# Revit family: vanity unit with 2 drawers for consoles with countertop basin ground
name_source: partatom
category: Furniture
units: mm (PartAtom-declared; Revit-internal decimal feet)

## family parameters
Always vertical = Yes
Cut with Voids When Loaded = No
OmniClass Number = 23.21.19.15.33.13
Room Calculation Point = No
Shared = Yes
Work Plane-Based = No

## types (48) — shared parameters
BIMOBJECT = Sanitary: Compound units
CATALOG = Hansgrohe
DESIGN = Germany
ETIM = EC011381 | Bathroom furniture set
IFC = Furnishing element
MASTERFORMAT = 12 35 30.23 | Bathroom Casework
Manufacturer = Hansgrohe
NBSYN = $BASENUMBER.-$ARTNR.-$OBERFLAECHE.-$SURFACE.-$LODLEVEL.
NN = Vanity Unit with 2 Drawers for consoles with countertop basin ground
OBJECTTYPE = Object (single object)
OMNICLASS = 23-21 19 15 33 13 | Residential Bathroom Specialty Casework
PRODUCTFAMILY = Xelu Q
PRODUCTGROUP = vanity unit
PRODUCTURL = https://pro.hansgrohe.com
REGIONSET = Worldwide
UNICLASS2015 = Pr_40_30_78_05 | Bathroom furniture
UNICLASS_2015_CODE = 40_30_78_05
UNIFORMATII = E2010 | Fixed Furnishings
UNSPSC = 56 | Furniture and Furnishings
etim7_EC011381 = EC011381

## per-type parameters (varying)
| type | ARTNR | BASENUMBER | GTINCODE | L | LINA | LODLEVEL | Model | NAME | NB | OBERFLAECHE | PERMALINK | SURFACE | WEIGHT |
| Vanity unit 1360_550 with 2 drawers for consoles with countertop basin ground-54066000-High Gloss White-CHROME-200 | 54066000 | Vanity unit 1360/550 with 2 drawers for consoles with countertop basin ground | 4059625456378 | 1360 | Vanity unit 1360/550 with 2 drawers for consoles with countertop basin ground-54066000-High Gloss White-CHROME-200 | 200 | Vanity unit 1360/550 with 2 drawers for consoles with countertop basin ground-54066000-High Gloss White-CHROME-200 | Xelu Q Vanity unit High Gloss White 1360/550 with 2 drawers for consoles with countertop basin ground | Vanity unit 1360/550 with 2 drawers for consoles with countertop basin ground-54066000-High Gloss White-CHROME-200 | High Gloss White | 54066XXX | CHROME | 45.1 |
| Vanity unit 1360_550 with 2 drawers for consoles with countertop basin ground-54066000-High Gloss White-CHROME-400 | 54066000 | Vanity unit 1360/550 with 2 drawers for consoles with countertop basin ground | 4059625456378 | 1360 | Vanity unit 1360/550 with 2 drawers for consoles with countertop basin ground-54066000-High Gloss White-CHROME-400 | 400 | Vanity unit 1360/550 with 2 drawers for consoles with countertop basin ground-54066000-High Gloss White-CHROME-400 | Xelu Q Vanity unit High Gloss White 1360/550 with 2 drawers for consoles with countertop basin ground | Vanity unit 1360/550 with 2 drawers for consoles with countertop basin ground-54066000-High Gloss White-CHROME-400 | High Gloss White | 54066XXX | CHROME | 45.1 |
| Vanity unit 1360_550 with 2 drawers for consoles with countertop basin ground-54066670-High Gloss White-MATT_BLACK-200 | 54066670 | Vanity unit 1360/550 with 2 drawers for consoles with countertop basin ground | 4059625456378 | 1360 | Vanity unit 1360/550 with 2 drawers for consoles with countertop basin ground-54066670-High Gloss White-MATT_BLACK-200 | 200 | Vanity unit 1360/550 with 2 drawers for consoles with countertop basin ground-54066670-High Gloss White-MATT_BLACK-200 | Xelu Q Vanity unit High Gloss White 1360/550 with 2 drawers for consoles with countertop basin ground | Vanity unit 1360/550 with 2 drawers for consoles with countertop basin ground-54066670-High Gloss White-MATT_BLACK-200 | High Gloss White | 54066XXX | MATT_BLACK | 45.1 |
| Vanity unit 1360_550 with 2 drawers for consoles with countertop basin ground-54066670-High Gloss White-MATT_BLACK-400 | 54066670 | Vanity unit 1360/550 with 2 drawers for consoles with countertop basin ground | 4059625456378 | 1360 | Vanity unit 1360/550 with 2 drawers for consoles with countertop basin ground-54066670-High Gloss White-MATT_BLACK-400 | 400 | Vanity unit 1360/550 with 2 drawers for consoles with countertop basin ground-54066670-High Gloss White-MATT_BLACK-400 | Xelu Q Vanity unit High Gloss White 1360/550 with 2 drawers for consoles with countertop basin ground | Vanity unit 1360/550 with 2 drawers for consoles with countertop basin ground-54066670-High Gloss White-MATT_BLACK-400 | High Gloss White | 54066XXX | MATT_BLACK | 45.1 |
| Vanity unit 1360_550 with 2 drawers for consoles with countertop basin ground-54066700-High Gloss White-MATT_WHITE-200 | 54066700 | Vanity unit 1360/550 with 2 drawers for consoles with countertop basin ground | 4059625456378 | 1360 | Vanity unit 1360/550 with 2 drawers for consoles with countertop basin ground-54066700-High Gloss White-MATT_WHITE-200 | 200 | Vanity unit 1360/550 with 2 drawers for consoles with countertop basin ground-54066700-High Gloss White-MATT_WHITE-200 | Xelu Q Vanity unit High Gloss White 1360/550 with 2 drawers for consoles with countertop basin ground | Vanity unit 1360/550 with 2 drawers for consoles with countertop basin ground-54066700-High Gloss White-MATT_WHITE-200 | High Gloss White | 54066XXX | MATT_WHITE | 45.1 |
| Vanity unit 1360_550 with 2 drawers for consoles with countertop basin ground-54066700-High Gloss White-MATT_WHITE-400 | 54066700 | Vanity unit 1360/550 with 2 drawers for consoles with countertop basin ground | 4059625456378 | 1360 | Vanity unit 1360/550 with 2 drawers for consoles with countertop basin ground-54066700-High Gloss White-MATT_WHITE-400 | 400 | Vanity unit 1360/550 with 2 drawers for consoles with countertop basin ground-54066700-High Gloss White-MATT_WHITE-400 | Xelu Q Vanity unit High Gloss White 1360/550 with 2 drawers for consoles with countertop basin ground | Vanity unit 1360/550 with 2 drawers for consoles with countertop basin ground-54066700-High Gloss White-MATT_WHITE-400 | High Gloss White | 54066XXX | MATT_WHITE | 45.1 |
| Vanity unit 1360_550 with 2 drawers for consoles with countertop basin ground-54067000-Diamond Matt Grey-CHROME-200 | 54067000 | Vanity unit 1360/550 with 2 drawers for consoles with countertop basin ground | 4059625456347 | 1360 | Vanity unit 1360/550 with 2 drawers for consoles with countertop basin ground-54067000-Diamond Matt Grey-CHROME-200 | 200 | Vanity unit 1360/550 with 2 drawers for consoles with countertop basin ground-54067000-Diamond Matt Grey-CHROME-200 | Xelu Q Vanity unit Diamond Matt Grey 1360/550 with 2 drawers for consoles with countertop basin ground | Vanity unit 1360/550 with 2 drawers for consoles with countertop basin ground-54067000-Diamond Matt Grey-CHROME-200 | Diamond Matt Grey | 54067XXX | CHROME | 45.1 |
| Vanity unit 1360_550 with 2 drawers for consoles with countertop basin ground-54067000-Diamond Matt Grey-CHROME-400 | 54067000 | Vanity unit 1360/550 with 2 drawers for consoles with countertop basin ground | 4059625456347 | 1360 | Vanity unit 1360/550 with 2 drawers for consoles with countertop basin ground-54067000-Diamond Matt Grey-CHROME-400 | 400 | Vanity unit 1360/550 with 2 drawers for consoles with countertop basin ground-54067000-Diamond Matt Grey-CHROME-400 | Xelu Q Vanity unit Diamond Matt Grey 1360/550 with 2 drawers for consoles with countertop basin ground | Vanity unit 1360/550 with 2 drawers for consoles with countertop basin ground-54067000-Diamond Matt Grey-CHROME-400 | Diamond Matt Grey | 54067XXX | CHROME | 45.1 |
| Vanity unit 1360_550 with 2 drawers for consoles with countertop basin ground-54067670-Diamond Matt Grey-MATT_BLACK-200 | 54067670 | Vanity unit 1360/550 with 2 drawers for consoles with countertop basin ground | 4059625456347 | 1360 | Vanity unit 1360/550 with 2 drawers for consoles with countertop basin ground-54067670-Diamond Matt Grey-MATT_BLACK-200 | 200 | Vanity unit 1360/550 with 2 drawers for consoles with countertop basin ground-54067670-Diamond Matt Grey-MATT_BLACK-200 | Xelu Q Vanity unit Diamond Matt Grey 1360/550 with 2 drawers for consoles with countertop basin ground | Vanity unit 1360/550 with 2 drawers for consoles with countertop basin ground-54067670-Diamond Matt Grey-MATT_BLACK-200 | Diamond Matt Grey | 54067XXX | MATT_BLACK | 45.1 |
| Vanity unit 1360_550 with 2 drawers for consoles with countertop basin ground-54067670-Diamond Matt Grey-MATT_BLACK-400 | 54067670 | Vanity unit 1360/550 with 2 drawers for consoles with countertop basin ground | 4059625456347 | 1360 | Vanity unit 1360/550 with 2 drawers for consoles with countertop basin ground-54067670-Diamond Matt Grey-MATT_BLACK-400 | 400 | Vanity unit 1360/550 with 2 drawers for consoles with countertop basin ground-54067670-Diamond Matt Grey-MATT_BLACK-400 | Xelu Q Vanity unit Diamond Matt Grey 1360/550 with 2 drawers for consoles with countertop basin ground | Vanity unit 1360/550 with 2 drawers for consoles with countertop basin ground-54067670-Diamond Matt Grey-MATT_BLACK-400 | Diamond Matt Grey | 54067XXX | MATT_BLACK | 45.1 |
| Vanity unit 1360_550 with 2 drawers for consoles with countertop basin ground-54067700-Diamond Matt Grey-MATT_WHITE-200 | 54067700 | Vanity unit 1360/550 with 2 drawers for consoles with countertop basin ground | 4059625456347 | 1360 | Vanity unit 1360/550 with 2 drawers for consoles with countertop basin ground-54067700-Diamond Matt Grey-MATT_WHITE-200 | 200 | Vanity unit 1360/550 with 2 drawers for consoles with countertop basin ground-54067700-Diamond Matt Grey-MATT_WHITE-200 | Xelu Q Vanity unit Diamond Matt Grey 1360/550 with 2 drawers for consoles with countertop basin ground | Vanity unit 1360/550 with 2 drawers for consoles with countertop basin ground-54067700-Diamond Matt Grey-MATT_WHITE-200 | Diamond Matt Grey | 54067XXX | MATT_WHITE | 45.1 |
| Vanity unit 1360_550 with 2 drawers for consoles with countertop basin ground-54067700-Diamond Matt Grey-MATT_WHITE-400 | 54067700 | Vanity unit 1360/550 with 2 drawers for consoles with countertop basin ground | 4059625456347 | 1360 | Vanity unit 1360/550 with 2 drawers for consoles with countertop basin ground-54067700-Diamond Matt Grey-MATT_WHITE-400 | 400 | Vanity unit 1360/550 with 2 drawers for consoles with countertop basin ground-54067700-Diamond Matt Grey-MATT_WHITE-400 | Xelu Q Vanity unit Diamond Matt Grey 1360/550 with 2 drawers for consoles with countertop basin ground | Vanity unit 1360/550 with 2 drawers for consoles with countertop basin ground-54067700-Diamond Matt Grey-MATT_WHITE-400 | Diamond Matt Grey | 54067XXX | MATT_WHITE | 45.1 |
| Vanity unit 1360_550 with 2 drawers for consoles with countertop basin ground-54068000-Natural Oak-CHROME-200 | 54068000 | Vanity unit 1360/550 with 2 drawers for consoles with countertop basin ground | 4059625456316 | 1360 | Vanity unit 1360/550 with 2 drawers for consoles with countertop basin ground-54068000-Natural Oak-CHROME-200 | 200 | Vanity unit 1360/550 with 2 drawers for consoles with countertop basin ground-54068000-Natural Oak-CHROME-200 | Xelu Q Vanity unit Natural Oak 1360/550 with 2 drawers for consoles with countertop basin ground | Vanity unit 1360/550 with 2 drawers for consoles with countertop basin ground-54068000-Natural Oak-CHROME-200 | Natural Oak | 54068XXX | CHROME | 45.1 |
| Vanity unit 1360_550 with 2 drawers for consoles with countertop basin ground-54068000-Natural Oak-CHROME-400 | 54068000 | Vanity unit 1360/550 with 2 drawers for consoles with countertop basin ground | 4059625456316 | 1360 | Vanity unit 1360/550 with 2 drawers for consoles with countertop basin ground-54068000-Natural Oak-CHROME-400 | 400 | Vanity unit 1360/550 with 2 drawers for consoles with countertop basin ground-54068000-Natural Oak-CHROME-400 | Xelu Q Vanity unit Natural Oak 1360/550 with 2 drawers for consoles with countertop basin ground | Vanity unit 1360/550 with 2 drawers for consoles with countertop basin ground-54068000-Natural Oak-CHROME-400 | Natural Oak | 54068XXX | CHROME | 45.1 |
| Vanity unit 1360_550 with 2 drawers for consoles with countertop basin ground-54068670-Natural Oak-MATT_BLACK-200 | 54068670 | Vanity unit 1360/550 with 2 drawers for consoles with countertop basin ground | 4059625456316 | 1360 | Vanity unit 1360/550 with 2 drawers for consoles with countertop basin ground-54068670-Natural Oak-MATT_BLACK-200 | 200 | Vanity unit 1360/550 with 2 drawers for consoles with countertop basin ground-54068670-Natural Oak-MATT_BLACK-200 | Xelu Q Vanity unit Natural Oak 1360/550 with 2 drawers for consoles with countertop basin ground | Vanity unit 1360/550 with 2 drawers for consoles with countertop basin ground-54068670-Natural Oak-MATT_BLACK-200 | Natural Oak | 54068XXX | MATT_BLACK | 45.1 |
| Vanity unit 1360_550 with 2 drawers for consoles with countertop basin ground-54068670-Natural Oak-MATT_BLACK-400 | 54068670 | Vanity unit 1360/550 with 2 drawers for consoles with countertop basin ground | 4059625456316 | 1360 | Vanity unit 1360/550 with 2 drawers for consoles with countertop basin ground-54068670-Natural Oak-MATT_BLACK-400 | 400 | Vanity unit 1360/550 with 2 drawers for consoles with countertop basin ground-54068670-Natural Oak-MATT_BLACK-400 | Xelu Q Vanity unit Natural Oak 1360/550 with 2 drawers for consoles with countertop basin ground | Vanity unit 1360/550 with 2 drawers for consoles with countertop basin ground-54068670-Natural Oak-MATT_BLACK-400 | Natural Oak | 54068XXX | MATT_BLACK | 45.1 |
| Vanity unit 1360_550 with 2 drawers for consoles with countertop basin ground-54068700-Natural Oak-MATT_WHITE-200 | 54068700 | Vanity unit 1360/550 with 2 drawers for consoles with countertop basin ground | 4059625456316 | 1360 | Vanity unit 1360/550 with 2 drawers for consoles with countertop basin ground-54068700-Natural Oak-MATT_WHITE-200 | 200 | Vanity unit 1360/550 with 2 drawers for consoles with countertop basin ground-54068700-Natural Oak-MATT_WHITE-200 | Xelu Q Vanity unit Natural Oak 1360/550 with 2 drawers for consoles with countertop basin ground | Vanity unit 1360/550 with 2 drawers for consoles with countertop basin ground-54068700-Natural Oak-MATT_WHITE-200 | Natural Oak | 54068XXX | MATT_WHITE | 45.1 |
| Vanity unit 1360_550 with 2 drawers for consoles with countertop basin ground-54068700-Natural Oak-MATT_WHITE-400 | 54068700 | Vanity unit 1360/550 with 2 drawers for consoles with countertop basin ground | 4059625456316 | 1360 | Vanity unit 1360/550 with 2 drawers for consoles with countertop basin ground-54068700-Natural Oak-MATT_WHITE-400 | 400 | Vanity unit 1360/550 with 2 drawers for consoles with countertop basin ground-54068700-Natural Oak-MATT_WHITE-400 | Xelu Q Vanity unit Natural Oak 1360/550 with 2 drawers for consoles with countertop basin ground | Vanity unit 1360/550 with 2 drawers for consoles with countertop basin ground-54068700-Natural Oak-MATT_WHITE-400 | Natural Oak | 54068XXX | MATT_WHITE | 45.1 |
| Vanity unit 1360_550 with 2 drawers for consoles with countertop basin ground-54069000-Dark Walnut-CHROME-200 | 54069000 | Vanity unit 1360/550 with 2 drawers for consoles with countertop basin ground | 4059625456286 | 1360 | Vanity unit 1360/550 with 2 drawers for consoles with countertop basin ground-54069000-Dark Walnut-CHROME-200 | 200 | Vanity unit 1360/550 with 2 drawers for consoles with countertop basin ground-54069000-Dark Walnut-CHROME-200 | Xelu Q Vanity unit Dark Walnut 1360/550 with 2 drawers for consoles with countertop basin ground | Vanity unit 1360/550 with 2 drawers for consoles with countertop basin ground-54069000-Dark Walnut-CHROME-200 | Dark Walnut | 54069XXX | CHROME | 45.1 |
| Vanity unit 1360_550 with 2 drawers for consoles with countertop basin ground-54069000-Dark Walnut-CHROME-400 | 54069000 | Vanity unit 1360/550 with 2 drawers for consoles with countertop basin ground | 4059625456286 | 1360 | Vanity unit 1360/550 with 2 drawers for consoles with countertop basin ground-54069000-Dark Walnut-CHROME-400 | 400 | Vanity unit 1360/550 with 2 drawers for consoles with countertop basin ground-54069000-Dark Walnut-CHROME-400 | Xelu Q Vanity unit Dark Walnut 1360/550 with 2 drawers for consoles with countertop basin ground | Vanity unit 1360/550 with 2 drawers for consoles with countertop basin ground-54069000-Dark Walnut-CHROME-400 | Dark Walnut | 54069XXX | CHROME | 45.1 |
| Vanity unit 1360_550 with 2 drawers for consoles with countertop basin ground-54069670-Dark Walnut-MATT_BLACK-200 | 54069670 | Vanity unit 1360/550 with 2 drawers for consoles with countertop basin ground | 4059625456286 | 1360 | Vanity unit 1360/550 with 2 drawers for consoles with countertop basin ground-54069670-Dark Walnut-MATT_BLACK-200 | 200 | Vanity unit 1360/550 with 2 drawers for consoles with countertop basin ground-54069670-Dark Walnut-MATT_BLACK-200 | Xelu Q Vanity unit Dark Walnut 1360/550 with 2 drawers for consoles with countertop basin ground | Vanity unit 1360/550 with 2 drawers for consoles with countertop basin ground-54069670-Dark Walnut-MATT_BLACK-200 | Dark Walnut | 54069XXX | MATT_BLACK | 45.1 |
| Vanity unit 1360_550 with 2 drawers for consoles with countertop basin ground-54069670-Dark Walnut-MATT_BLACK-400 | 54069670 | Vanity unit 1360/550 with 2 drawers for consoles with countertop basin ground | 4059625456286 | 1360 | Vanity unit 1360/550 with 2 drawers for consoles with countertop basin ground-54069670-Dark Walnut-MATT_BLACK-400 | 400 | Vanity unit 1360/550 with 2 drawers for consoles with countertop basin ground-54069670-Dark Walnut-MATT_BLACK-400 | Xelu Q Vanity unit Dark Walnut 1360/550 with 2 drawers for consoles with countertop basin ground | Vanity unit 1360/550 with 2 drawers for consoles with countertop basin ground-54069670-Dark Walnut-MATT_BLACK-400 | Dark Walnut | 54069XXX | MATT_BLACK | 45.1 |
| Vanity unit 1360_550 with 2 drawers for consoles with countertop basin ground-54069700-Dark Walnut-MATT_WHITE-200 | 54069700 | Vanity unit 1360/550 with 2 drawers for consoles with countertop basin ground | 4059625456286 | 1360 | Vanity unit 1360/550 with 2 drawers for consoles with countertop basin ground-54069700-Dark Walnut-MATT_WHITE-200 | 200 | Vanity unit 1360/550 with 2 drawers for consoles with countertop basin ground-54069700-Dark Walnut-MATT_WHITE-200 | Xelu Q Vanity unit Dark Walnut 1360/550 with 2 drawers for consoles with countertop basin ground | Vanity unit 1360/550 with 2 drawers for consoles with countertop basin ground-54069700-Dark Walnut-MATT_WHITE-200 | Dark Walnut | 54069XXX | MATT_WHITE | 45.1 |
| Vanity unit 1360_550 with 2 drawers for consoles with countertop basin ground-54069700-Dark Walnut-MATT_WHITE-400 | 54069700 | Vanity unit 1360/550 with 2 drawers for consoles with countertop basin ground | 4059625456286 | 1360 | Vanity unit 1360/550 with 2 drawers for consoles with countertop basin ground-54069700-Dark Walnut-MATT_WHITE-400 | 400 | Vanity unit 1360/550 with 2 drawers for consoles with countertop basin ground-54069700-Dark Walnut-MATT_WHITE-400 | Xelu Q Vanity unit Dark Walnut 1360/550 with 2 drawers for consoles with countertop basin ground | Vanity unit 1360/550 with 2 drawers for consoles with countertop basin ground-54069700-Dark Walnut-MATT_WHITE-400 | Dark Walnut | 54069XXX | MATT_WHITE | 45.1 |
| Vanity unit 1560_550 with 2 drawers for consoles with countertop basin ground-54070000-High Gloss White-CHROME-200 | 54070000 | Vanity unit 1560/550 with 2 drawers for consoles with countertop basin ground | 4059625456255 | 1560 | Vanity unit 1560/550 with 2 drawers for consoles with countertop basin ground-54070000-High Gloss White-CHROME-200 | 200 | Vanity unit 1560/550 with 2 drawers for consoles with countertop basin ground-54070000-High Gloss White-CHROME-200 | Xelu Q Vanity unit High Gloss White 1560/550 with 2 drawers for consoles with countertop basin ground | Vanity unit 1560/550 with 2 drawers for consoles with countertop basin ground-54070000-High Gloss White-CHROME-200 | High Gloss White | 54070XXX | CHROME | 49.1 |
| Vanity unit 1560_550 with 2 drawers for consoles with countertop basin ground-54070000-High Gloss White-CHROME-400 | 54070000 | Vanity unit 1560/550 with 2 drawers for consoles with countertop basin ground | 4059625456255 | 1560 | Vanity unit 1560/550 with 2 drawers for consoles with countertop basin ground-54070000-High Gloss White-CHROME-400 | 400 | Vanity unit 1560/550 with 2 drawers for consoles with countertop basin ground-54070000-High Gloss White-CHROME-400 | Xelu Q Vanity unit High Gloss White 1560/550 with 2 drawers for consoles with countertop basin ground | Vanity unit 1560/550 with 2 drawers for consoles with countertop basin ground-54070000-High Gloss White-CHROME-400 | High Gloss White | 54070XXX | CHROME | 49.1 |
| Vanity unit 1560_550 with 2 drawers for consoles with countertop basin ground-54070670-High Gloss White-MATT_BLACK-200 | 54070670 | Vanity unit 1560/550 with 2 drawers for consoles with countertop basin ground | 4059625456255 | 1560 | Vanity unit 1560/550 with 2 drawers for consoles with countertop basin ground-54070670-High Gloss White-MATT_BLACK-200 | 200 | Vanity unit 1560/550 with 2 drawers for consoles with countertop basin ground-54070670-High Gloss White-MATT_BLACK-200 | Xelu Q Vanity unit High Gloss White 1560/550 with 2 drawers for consoles with countertop basin ground | Vanity unit 1560/550 with 2 drawers for consoles with countertop basin ground-54070670-High Gloss White-MATT_BLACK-200 | High Gloss White | 54070XXX | MATT_BLACK | 49.1 |
| Vanity unit 1560_550 with 2 drawers for consoles with countertop basin ground-54070670-High Gloss White-MATT_BLACK-400 | 54070670 | Vanity unit 1560/550 with 2 drawers for consoles with countertop basin ground | 4059625456255 | 1560 | Vanity unit 1560/550 with 2 drawers for consoles with countertop basin ground-54070670-High Gloss White-MATT_BLACK-400 | 400 | Vanity unit 1560/550 with 2 drawers for consoles with countertop basin ground-54070670-High Gloss White-MATT_BLACK-400 | Xelu Q Vanity unit High Gloss White 1560/550 with 2 drawers for consoles with countertop basin ground | Vanity unit 1560/550 with 2 drawers for consoles with countertop basin ground-54070670-High Gloss White-MATT_BLACK-400 | High Gloss White | 54070XXX | MATT_BLACK | 49.1 |
| Vanity unit 1560_550 with 2 drawers for consoles with countertop basin ground-54070700-High Gloss White-MATT_WHITE-200 | 54070700 | Vanity unit 1560/550 with 2 drawers for consoles with countertop basin ground | 4059625456255 | 1560 | Vanity unit 1560/550 with 2 drawers for consoles with countertop basin ground-54070700-High Gloss White-MATT_WHITE-200 | 200 | Vanity unit 1560/550 with 2 drawers for consoles with countertop basin ground-54070700-High Gloss White-MATT_WHITE-200 | Xelu Q Vanity unit High Gloss White 1560/550 with 2 drawers for consoles with countertop basin ground | Vanity unit 1560/550 with 2 drawers for consoles with countertop basin ground-54070700-High Gloss White-MATT_WHITE-200 | High Gloss White | 54070XXX | MATT_WHITE | 49.1 |
| Vanity unit 1560_550 with 2 drawers for consoles with countertop basin ground-54070700-High Gloss White-MATT_WHITE-400 | 54070700 | Vanity unit 1560/550 with 2 drawers for consoles with countertop basin ground | 4059625456255 | 1560 | Vanity unit 1560/550 with 2 drawers for consoles with countertop basin ground-54070700-High Gloss White-MATT_WHITE-400 | 400 | Vanity unit 1560/550 with 2 drawers for consoles with countertop basin ground-54070700-High Gloss White-MATT_WHITE-400 | Xelu Q Vanity unit High Gloss White 1560/550 with 2 drawers for consoles with countertop basin ground | Vanity unit 1560/550 with 2 drawers for consoles with countertop basin ground-54070700-High Gloss White-MATT_WHITE-400 | High Gloss White | 54070XXX | MATT_WHITE | 49.1 |
| Vanity unit 1560_550 with 2 drawers for consoles with countertop basin ground-54071000-Diamond Matt Grey-CHROME-200 | 54071000 | Vanity unit 1560/550 with 2 drawers for consoles with countertop basin ground | 4059625456620 | 1560 | Vanity unit 1560/550 with 2 drawers for consoles with countertop basin ground-54071000-Diamond Matt Grey-CHROME-200 | 200 | Vanity unit 1560/550 with 2 drawers for consoles with countertop basin ground-54071000-Diamond Matt Grey-CHROME-200 | Xelu Q Vanity unit Diamond Matt Grey 1560/550 with 2 drawers for consoles with countertop basin ground | Vanity unit 1560/550 with 2 drawers for consoles with countertop basin ground-54071000-Diamond Matt Grey-CHROME-200 | Diamond Matt Grey | 54071XXX | CHROME | 49.1 |
| Vanity unit 1560_550 with 2 drawers for consoles with countertop basin ground-54071000-Diamond Matt Grey-CHROME-400 | 54071000 | Vanity unit 1560/550 with 2 drawers for consoles with countertop basin ground | 4059625456620 | 1560 | Vanity unit 1560/550 with 2 drawers for consoles with countertop basin ground-54071000-Diamond Matt Grey-CHROME-400 | 400 | Vanity unit 1560/550 with 2 drawers for consoles with countertop basin ground-54071000-Diamond Matt Grey-CHROME-400 | Xelu Q Vanity unit Diamond Matt Grey 1560/550 with 2 drawers for consoles with countertop basin ground | Vanity unit 1560/550 with 2 drawers for consoles with countertop basin ground-54071000-Diamond Matt Grey-CHROME-400 | Diamond Matt Grey | 54071XXX | CHROME | 49.1 |
| Vanity unit 1560_550 with 2 drawers for consoles with countertop basin ground-54071670-Diamond Matt Grey-MATT_BLACK-200 | 54071670 | Vanity unit 1560/550 with 2 drawers for consoles with countertop basin ground | 4059625456620 | 1560 | Vanity unit 1560/550 with 2 drawers for consoles with countertop basin ground-54071670-Diamond Matt Grey-MATT_BLACK-200 | 200 | Vanity unit 1560/550 with 2 drawers for consoles with countertop basin ground-54071670-Diamond Matt Grey-MATT_BLACK-200 | Xelu Q Vanity unit Diamond Matt Grey 1560/550 with 2 drawers for consoles with countertop basin ground | Vanity unit 1560/550 with 2 drawers for consoles with countertop basin ground-54071670-Diamond Matt Grey-MATT_BLACK-200 | Diamond Matt Grey | 54071XXX | MATT_BLACK | 49.1 |
| Vanity unit 1560_550 with 2 drawers for consoles with countertop basin ground-54071670-Diamond Matt Grey-MATT_BLACK-400 | 54071670 | Vanity unit 1560/550 with 2 drawers for consoles with countertop basin ground | 4059625456620 | 1560 | Vanity unit 1560/550 with 2 drawers for consoles with countertop basin ground-54071670-Diamond Matt Grey-MATT_BLACK-400 | 400 | Vanity unit 1560/550 with 2 drawers for consoles with countertop basin ground-54071670-Diamond Matt Grey-MATT_BLACK-400 | Xelu Q Vanity unit Diamond Matt Grey 1560/550 with 2 drawers for consoles with countertop basin ground | Vanity unit 1560/550 with 2 drawers for consoles with countertop basin ground-54071670-Diamond Matt Grey-MATT_BLACK-400 | Diamond Matt Grey | 54071XXX | MATT_BLACK | 49.1 |
| Vanity unit 1560_550 with 2 drawers for consoles with countertop basin ground-54071700-Diamond Matt Grey-MATT_WHITE-200 | 54071700 | Vanity unit 1560/550 with 2 drawers for consoles with countertop basin ground | 4059625456620 | 1560 | Vanity unit 1560/550 with 2 drawers for consoles with countertop basin ground-54071700-Diamond Matt Grey-MATT_WHITE-200 | 200 | Vanity unit 1560/550 with 2 drawers for consoles with countertop basin ground-54071700-Diamond Matt Grey-MATT_WHITE-200 | Xelu Q Vanity unit Diamond Matt Grey 1560/550 with 2 drawers for consoles with countertop basin ground | Vanity unit 1560/550 with 2 drawers for consoles with countertop basin ground-54071700-Diamond Matt Grey-MATT_WHITE-200 | Diamond Matt Grey | 54071XXX | MATT_WHITE | 49.1 |
| Vanity unit 1560_550 with 2 drawers for consoles with countertop basin ground-54071700-Diamond Matt Grey-MATT_WHITE-400 | 54071700 | Vanity unit 1560/550 with 2 drawers for consoles with countertop basin ground | 4059625456620 | 1560 | Vanity unit 1560/550 with 2 drawers for consoles with countertop basin ground-54071700-Diamond Matt Grey-MATT_WHITE-400 | 400 | Vanity unit 1560/550 with 2 drawers for consoles with countertop basin ground-54071700-Diamond Matt Grey-MATT_WHITE-400 | Xelu Q Vanity unit Diamond Matt Grey 1560/550 with 2 drawers for consoles with countertop basin ground | Vanity unit 1560/550 with 2 drawers for consoles with countertop basin ground-54071700-Diamond Matt Grey-MATT_WHITE-400 | Diamond Matt Grey | 54071XXX | MATT_WHITE | 49.1 |
| Vanity unit 1560_550 with 2 drawers for consoles with countertop basin ground-54072000-Natural Oak-CHROME-200 | 54072000 | Vanity unit 1560/550 with 2 drawers for consoles with countertop basin ground | 4059625456590 | 1560 | Vanity unit 1560/550 with 2 drawers for consoles with countertop basin ground-54072000-Natural Oak-CHROME-200 | 200 | Vanity unit 1560/550 with 2 drawers for consoles with countertop basin ground-54072000-Natural Oak-CHROME-200 | Xelu Q Vanity unit Natural Oak 1560/550 with 2 drawers for consoles with countertop basin ground | Vanity unit 1560/550 with 2 drawers for consoles with countertop basin ground-54072000-Natural Oak-CHROME-200 | Natural Oak | 54072XXX | CHROME | 49.1 |
| Vanity unit 1560_550 with 2 drawers for consoles with countertop basin ground-54072000-Natural Oak-CHROME-400 | 54072000 | Vanity unit 1560/550 with 2 drawers for consoles with countertop basin ground | 4059625456590 | 1560 | Vanity unit 1560/550 with 2 drawers for consoles with countertop basin ground-54072000-Natural Oak-CHROME-400 | 400 | Vanity unit 1560/550 with 2 drawers for consoles with countertop basin ground-54072000-Natural Oak-CHROME-400 | Xelu Q Vanity unit Natural Oak 1560/550 with 2 drawers for consoles with countertop basin ground | Vanity unit 1560/550 with 2 drawers for consoles with countertop basin ground-54072000-Natural Oak-CHROME-400 | Natural Oak | 54072XXX | CHROME | 49.1 |
| Vanity unit 1560_550 with 2 drawers for consoles with countertop basin ground-54072670-Natural Oak-MATT_BLACK-200 | 54072670 | Vanity unit 1560/550 with 2 drawers for consoles with countertop basin ground | 4059625456590 | 1560 | Vanity unit 1560/550 with 2 drawers for consoles with countertop basin ground-54072670-Natural Oak-MATT_BLACK-200 | 200 | Vanity unit 1560/550 with 2 drawers for consoles with countertop basin ground-54072670-Natural Oak-MATT_BLACK-200 | Xelu Q Vanity unit Natural Oak 1560/550 with 2 drawers for consoles with countertop basin ground | Vanity unit 1560/550 with 2 drawers for consoles with countertop basin ground-54072670-Natural Oak-MATT_BLACK-200 | Natural Oak | 54072XXX | MATT_BLACK | 49.1 |
| Vanity unit 1560_550 with 2 drawers for consoles with countertop basin ground-54072670-Natural Oak-MATT_BLACK-400 | 54072670 | Vanity unit 1560/550 with 2 drawers for consoles with countertop basin ground | 4059625456590 | 1560 | Vanity unit 1560/550 with 2 drawers for consoles with countertop basin ground-54072670-Natural Oak-MATT_BLACK-400 | 400 | Vanity unit 1560/550 with 2 drawers for consoles with countertop basin ground-54072670-Natural Oak-MATT_BLACK-400 | Xelu Q Vanity unit Natural Oak 1560/550 with 2 drawers for consoles with countertop basin ground | Vanity unit 1560/550 with 2 drawers for consoles with countertop basin ground-54072670-Natural Oak-MATT_BLACK-400 | Natural Oak | 54072XXX | MATT_BLACK | 49.1 |
| Vanity unit 1560_550 with 2 drawers for consoles with countertop basin ground-54072700-Natural Oak-MATT_WHITE-200 | 54072700 | Vanity unit 1560/550 with 2 drawers for consoles with countertop basin ground | 4059625456590 | 1560 | Vanity unit 1560/550 with 2 drawers for consoles with countertop basin ground-54072700-Natural Oak-MATT_WHITE-200 | 200 | Vanity unit 1560/550 with 2 drawers for consoles with countertop basin ground-54072700-Natural Oak-MATT_WHITE-200 | Xelu Q Vanity unit Natural Oak 1560/550 with 2 drawers for consoles with countertop basin ground | Vanity unit 1560/550 with 2 drawers for consoles with countertop basin ground-54072700-Natural Oak-MATT_WHITE-200 | Natural Oak | 54072XXX | MATT_WHITE | 49.1 |
| Vanity unit 1560_550 with 2 drawers for consoles with countertop basin ground-54072700-Natural Oak-MATT_WHITE-400 | 54072700 | Vanity unit 1560/550 with 2 drawers for consoles with countertop basin ground | 4059625456590 | 1560 | Vanity unit 1560/550 with 2 drawers for consoles with countertop basin ground-54072700-Natural Oak-MATT_WHITE-400 | 400 | Vanity unit 1560/550 with 2 drawers for consoles with countertop basin ground-54072700-Natural Oak-MATT_WHITE-400 | Xelu Q Vanity unit Natural Oak 1560/550 with 2 drawers for consoles with countertop basin ground | Vanity unit 1560/550 with 2 drawers for consoles with countertop basin ground-54072700-Natural Oak-MATT_WHITE-400 | Natural Oak | 54072XXX | MATT_WHITE | 49.1 |
| Vanity unit 1560_550 with 2 drawers for consoles with countertop basin ground-54073000-Dark Walnut-CHROME-200 | 54073000 | Vanity unit 1560/550 with 2 drawers for consoles with countertop basin ground | 4059625456569 | 1560 | Vanity unit 1560/550 with 2 drawers for consoles with countertop basin ground-54073000-Dark Walnut-CHROME-200 | 200 | Vanity unit 1560/550 with 2 drawers for consoles with countertop basin ground-54073000-Dark Walnut-CHROME-200 | Xelu Q Vanity unit Dark Walnut 1560/550 with 2 drawers for consoles with countertop basin ground | Vanity unit 1560/550 with 2 drawers for consoles with countertop basin ground-54073000-Dark Walnut-CHROME-200 | Dark Walnut | 54073XXX | CHROME | 49.1 |
| Vanity unit 1560_550 with 2 drawers for consoles with countertop basin ground-54073000-Dark Walnut-CHROME-400 | 54073000 | Vanity unit 1560/550 with 2 drawers for consoles with countertop basin ground | 4059625456569 | 1560 | Vanity unit 1560/550 with 2 drawers for consoles with countertop basin ground-54073000-Dark Walnut-CHROME-400 | 400 | Vanity unit 1560/550 with 2 drawers for consoles with countertop basin ground-54073000-Dark Walnut-CHROME-400 | Xelu Q Vanity unit Dark Walnut 1560/550 with 2 drawers for consoles with countertop basin ground | Vanity unit 1560/550 with 2 drawers for consoles with countertop basin ground-54073000-Dark Walnut-CHROME-400 | Dark Walnut | 54073XXX | CHROME | 49.1 |
| Vanity unit 1560_550 with 2 drawers for consoles with countertop basin ground-54073670-Dark Walnut-MATT_BLACK-200 | 54073670 | Vanity unit 1560/550 with 2 drawers for consoles with countertop basin ground | 4059625456569 | 1560 | Vanity unit 1560/550 with 2 drawers for consoles with countertop basin ground-54073670-Dark Walnut-MATT_BLACK-200 | 200 | Vanity unit 1560/550 with 2 drawers for consoles with countertop basin ground-54073670-Dark Walnut-MATT_BLACK-200 | Xelu Q Vanity unit Dark Walnut 1560/550 with 2 drawers for consoles with countertop basin ground | Vanity unit 1560/550 with 2 drawers for consoles with countertop basin ground-54073670-Dark Walnut-MATT_BLACK-200 | Dark Walnut | 54073XXX | MATT_BLACK | 49.1 |
| Vanity unit 1560_550 with 2 drawers for consoles with countertop basin ground-54073670-Dark Walnut-MATT_BLACK-400 | 54073670 | Vanity unit 1560/550 with 2 drawers for consoles with countertop basin ground | 4059625456569 | 1560 | Vanity unit 1560/550 with 2 drawers for consoles with countertop basin ground-54073670-Dark Walnut-MATT_BLACK-400 | 400 | Vanity unit 1560/550 with 2 drawers for consoles with countertop basin ground-54073670-Dark Walnut-MATT_BLACK-400 | Xelu Q Vanity unit Dark Walnut 1560/550 with 2 drawers for consoles with countertop basin ground | Vanity unit 1560/550 with 2 drawers for consoles with countertop basin ground-54073670-Dark Walnut-MATT_BLACK-400 | Dark Walnut | 54073XXX | MATT_BLACK | 49.1 |
| Vanity unit 1560_550 with 2 drawers for consoles with countertop basin ground-54073700-Dark Walnut-MATT_WHITE-200 | 54073700 | Vanity unit 1560/550 with 2 drawers for consoles with countertop basin ground | 4059625456569 | 1560 | Vanity unit 1560/550 with 2 drawers for consoles with countertop basin ground-54073700-Dark Walnut-MATT_WHITE-200 | 200 | Vanity unit 1560/550 with 2 drawers for consoles with countertop basin ground-54073700-Dark Walnut-MATT_WHITE-200 | Xelu Q Vanity unit Dark Walnut 1560/550 with 2 drawers for consoles with countertop basin ground | Vanity unit 1560/550 with 2 drawers for consoles with countertop basin ground-54073700-Dark Walnut-MATT_WHITE-200 | Dark Walnut | 54073XXX | MATT_WHITE | 49.1 |
| Vanity unit 1560_550 with 2 drawers for consoles with countertop basin ground-54073700-Dark Walnut-MATT_WHITE-400 | 54073700 | Vanity unit 1560/550 with 2 drawers for consoles with countertop basin ground | 4059625456569 | 1560 | Vanity unit 1560/550 with 2 drawers for consoles with countertop basin ground-54073700-Dark Walnut-MATT_WHITE-400 | 400 | Vanity unit 1560/550 with 2 drawers for consoles with countertop basin ground-54073700-Dark Walnut-MATT_WHITE-400 | Xelu Q Vanity unit Dark Walnut 1560/550 with 2 drawers for consoles with countertop basin ground | Vanity unit 1560/550 with 2 drawers for consoles with countertop basin ground-54073700-Dark Walnut-MATT_WHITE-400 | Dark Walnut | 54073XXX | MATT_WHITE | 49.1 |

type visibility flags: 48 boolean params named "<type name>_RX0RY0RZ0TX0TY0TZ0_V" — each type sets only its own to Yes (folded from table)

## geometry (parser evidence)
native form markers: Sweep x118
no freeform markers — native parametric forms only
